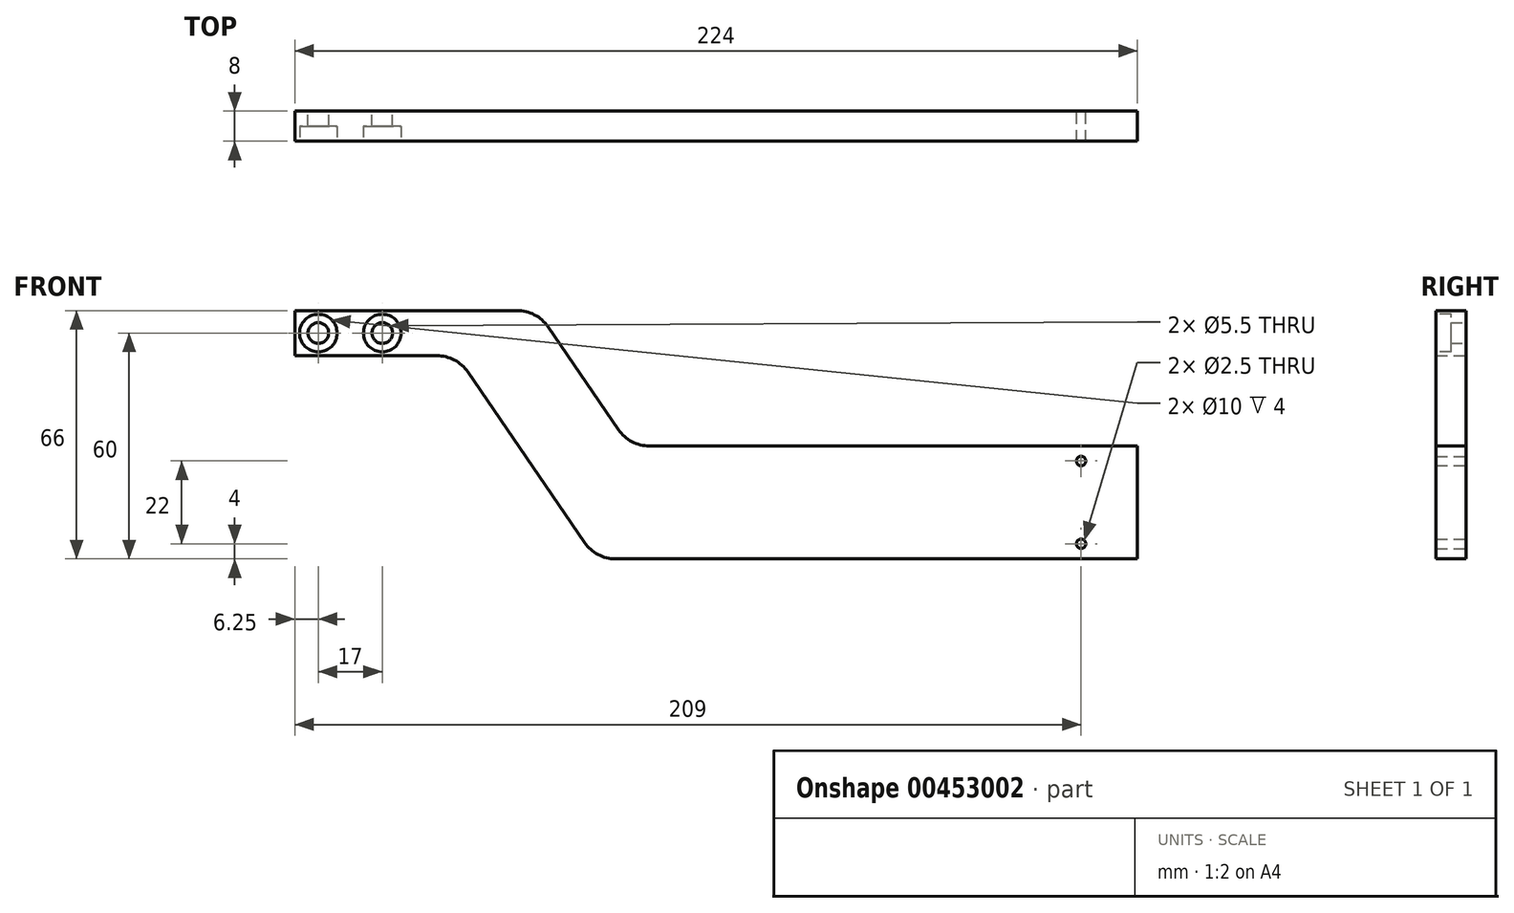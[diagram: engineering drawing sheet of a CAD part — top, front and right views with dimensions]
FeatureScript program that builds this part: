
annotation { "Feature Type Name" : "Feature", "Feature Type Description" : "" }
export const myFeature = defineFeature(function(context is Context, id is Id, definition is map)
    precondition{}
    {
        {
            var Q0;
            Q0=qCreatedBy(makeId("Front.planeOp"),FACE);
            var sketch = newSketch(context, id + "F0", { "sketchPlane" : qUnion([Q0])});
            skLineSegment(sketch, "E0.top", {"start": v(67.5, 15) * mm, "end": v(-62.23, 15) * mm});
            skLineSegment(sketch, "E0.left", {"start": v(67.5, -15) * mm, "end": v(67.5, 15) * mm});
            skPoint(sketch, "E0.middle", {"position": v(0, 0) * mm});
            skLineSegment(sketch, "E1", {"start": v(-70.48, 19.35) * mm, "end": v(-89.19, 46.65) * mm});
            skLineSegment(sketch, "E2", {"start": v(-97.44, 51) * mm, "end": v(-156.5, 51) * mm});
            skLineSegment(sketch, "E3", {"start": v(-156.5, 51) * mm, "end": v(-156.5, 39) * mm});
            skLineSegment(sketch, "E4", {"start": v(-156.5, 39) * mm, "end": v(-118.77, 39) * mm});
            skLineSegment(sketch, "E5", {"start": v(67.5, -15) * mm, "end": v(-71.23, -15) * mm});
            skLineSegment(sketch, "E6", {"start": v(-79.48, -10.65) * mm, "end": v(-110.52, 34.65) * mm});
            skPoint(sketch, "E7.visualSharp", {"position": v(-76.5, -15) * mm});
            skPoint(sketch, "E8.visualSharp", {"position": v(-113.5, 39) * mm});
            skPoint(sketch, "E9.visualSharp", {"position": v(-92.17, 51) * mm});
            skPoint(sketch, "E10.visualSharp", {"position": v(-67.5, 15) * mm});
            skLineSegment(sketch, "E11", {"start": v(-156.5, 45) * mm, "end": v(-109.27, 45) * mm, "construction": true});
            skCircle(sketch, "E12", {"center": v(-150.25, 45) * mm, "radius": 2.75 * mm});
            skCircle(sketch, "E13", {"center": v(-133.25, 45) * mm, "radius": 2.75 * mm});
            skCircle(sketch, "E14", {"center": v(52.5, 11) * mm, "radius": 1.25 * mm});
            skCircle(sketch, "E15", {"center": v(52.5, -11) * mm, "radius": 1.25 * mm});
            skArc(sketch, "E16.filletArc", {"start": v(-89.19, 46.65) * mm, "mid": v(-92.77, 49.85) * mm, "end": v(-97.44, 51) * mm});
            skArc(sketch, "E17.filletArc", {"start": v(-110.52, 34.65) * mm, "mid": v(-114.1, 37.85) * mm, "end": v(-118.77, 39) * mm});
            skArc(sketch, "E18.filletArc", {"start": v(-79.48, -10.65) * mm, "mid": v(-75.9, -13.85) * mm, "end": v(-71.23, -15) * mm});
            skArc(sketch, "E19.filletArc", {"start": v(-70.48, 19.35) * mm, "mid": v(-66.9, 16.15) * mm, "end": v(-62.23, 15) * mm});
            skSolve(sketch);
        }
        {
            var Q0;
            Q0=makeQuery(id+"F0.imprint","IMPRINT",FACE,{"disambiguationData":[TD([[makeQuery(id+"F0.imprint","IMPRINT",EDGE,{"derivedFrom":sQuery(id+"F0.wireOp",EDGE,"E0.top")}),1.0]])]});
            extrude(context, id + "F1", {"entities" : qUnion([Q0]), "depth" : 8 * mm});
        }
        {
            var Q0;
            Q0=makeQuery(id+"F1.opExtrude","CAP_FACE",FACE,{"disambiguationData":[OSD([sQuery(id+"F0.wireOp",EDGE,"E0.top"),sQuery(id+"F0.wireOp",EDGE,"E0.left"),sQuery(id+"F0.wireOp",EDGE,"E1"),sQuery(id+"F0.wireOp",EDGE,"E2"),sQuery(id+"F0.wireOp",EDGE,"E3"),sQuery(id+"F0.wireOp",EDGE,"E4"),sQuery(id+"F0.wireOp",EDGE,"E5"),sQuery(id+"F0.wireOp",EDGE,"E6"),sQuery(id+"F0.wireOp",EDGE,"E7.filletArc"),sQuery(id+"F0.wireOp",EDGE,"E8.filletArc"),sQuery(id+"F0.wireOp",EDGE,"E9.filletArc"),sQuery(id+"F0.wireOp",EDGE,"E10.filletArc"),sQuery(id+"F0.wireOp",EDGE,"E12"),sQuery(id+"F0.wireOp",EDGE,"E13"),sQuery(id+"F0.wireOp",EDGE,"E14"),sQuery(id+"F0.wireOp",EDGE,"E15")])],"isStart":false});
            var sketch = newSketch(context, id + "F2", { "sketchPlane" : qUnion([Q0])});
            skCircle(sketch, "E20", {"center": v(-150.25, 45) * mm, "radius": 5 * mm});
            skCircle(sketch, "E21", {"center": v(-133.25, 45) * mm, "radius": 5 * mm});
            skSolve(sketch);
        }
        {
            var Q0;
            Q0=makeQuery(id+"F2.imprint","IMPRINT",FACE,{"disambiguationData":[TD([[makeQuery(id+"F2.imprint","IMPRINT",EDGE,{"derivedFrom":sQuery(id+"F2.wireOp",EDGE,"E20")}),1.0]])]});
            var Q1;
            Q1=makeQuery(id+"F2.imprint","IMPRINT",FACE,{"disambiguationData":[TD([[makeQuery(id+"F2.imprint","IMPRINT",EDGE,{"derivedFrom":sQuery(id+"F2.wireOp",EDGE,"E21")}),1.0]])]});
            extrude(context, id + "F3", {"entities" : qUnion([Q0, Q1]), "operationType" : NewBodyOperationType.REMOVE, "oppositeDirection" : true, "depth" : 4 * mm});
        }
    });
